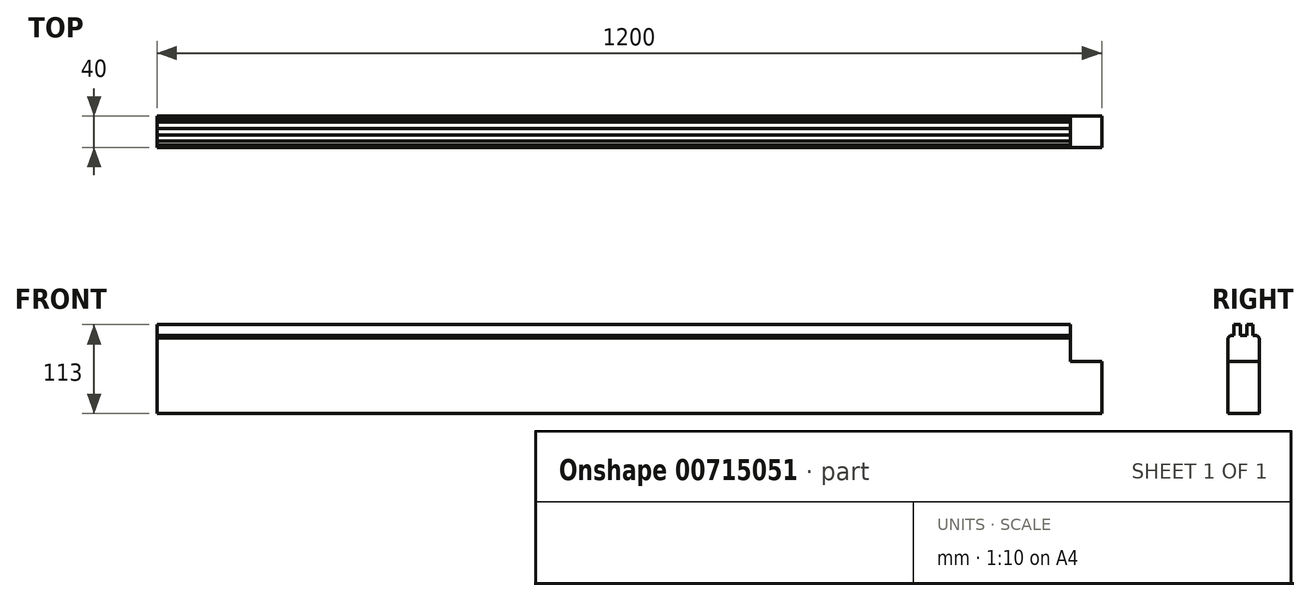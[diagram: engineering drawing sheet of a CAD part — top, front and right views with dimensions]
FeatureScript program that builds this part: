
annotation { "Feature Type Name" : "Feature", "Feature Type Description" : "" }
export const myFeature = defineFeature(function(context is Context, id is Id, definition is map)
    precondition{}
    {
        {
            assignVariable(context, id + "F0", {"name" : "Laenge", "anyValue" : 1200});
        }
        {
            var Q0;
            Q0=qCreatedBy(makeId("Right.planeOp"),FACE);
            var sketch = newSketch(context, id + "F1", { "sketchPlane" : qUnion([Q0])});
            skLineSegment(sketch, "E0", {"start": v(20, 63) * mm, "end": v(20, -63) * mm});
            skLineSegment(sketch, "E1", {"start": v(20, -63) * mm, "end": v(17, -66) * mm});
            skLineSegment(sketch, "E2", {"start": v(17, -66) * mm, "end": v(12, -66) * mm});
            skLineSegment(sketch, "E3", {"start": v(12, -52) * mm, "end": v(12, -66) * mm});
            skLineSegment(sketch, "E4", {"start": v(12, -52) * mm, "end": v(4, -52) * mm});
            skLineSegment(sketch, "E5", {"start": v(4, -66) * mm, "end": v(4, -52) * mm});
            skLineSegment(sketch, "E6", {"start": v(4, -66) * mm, "end": v(-4, -66) * mm});
            skLineSegment(sketch, "E7", {"start": v(-4, -52) * mm, "end": v(-4, -66) * mm});
            skLineSegment(sketch, "E8", {"start": v(-4, -52) * mm, "end": v(-12, -52) * mm});
            skLineSegment(sketch, "E9", {"start": v(-12, -66) * mm, "end": v(-12, -52) * mm});
            skLineSegment(sketch, "E10", {"start": v(-12, -66) * mm, "end": v(-17, -66) * mm});
            skLineSegment(sketch, "E11", {"start": v(-17, -66) * mm, "end": v(-20, -63) * mm});
            skLineSegment(sketch, "E12", {"start": v(-20, -63) * mm, "end": v(-20, 63) * mm});
            skLineSegment(sketch, "E13", {"start": v(-20, 63) * mm, "end": v(-17, 66) * mm});
            skLineSegment(sketch, "E14", {"start": v(-17, 66) * mm, "end": v(-12, 66) * mm});
            skLineSegment(sketch, "E15", {"start": v(-4, 66) * mm, "end": v(4, 66) * mm});
            skLineSegment(sketch, "E16", {"start": v(12, 66) * mm, "end": v(17, 66) * mm});
            skLineSegment(sketch, "E17", {"start": v(17, 66) * mm, "end": v(20, 63) * mm});
            skPoint(sketch, "E18.end.orphan", {"position": v(12, 57.8) * mm});
            skPoint(sketch, "E19.end.orphan", {"position": v(4, 66.3) * mm});
            skPoint(sketch, "E20.end.orphan", {"position": v(-4, 66.3) * mm});
            skLineSegment(sketch, "E21", {"start": v(-12, 66) * mm, "end": v(-12, 80) * mm});
            skLineSegment(sketch, "E22", {"start": v(-12, 80) * mm, "end": v(-4, 80) * mm});
            skLineSegment(sketch, "E23", {"start": v(-4, 80) * mm, "end": v(-4, 66) * mm});
            skLineSegment(sketch, "E24", {"start": v(4, 66) * mm, "end": v(4, 80) * mm});
            skLineSegment(sketch, "E25", {"start": v(4, 80) * mm, "end": v(12, 80) * mm});
            skLineSegment(sketch, "E26", {"start": v(12, 80) * mm, "end": v(12, 66) * mm});
            skLineSegment(sketch, "E27", {"start": v(20, -33) * mm, "end": v(-20, -33) * mm});
            skLineSegment(sketch, "E28", {"start": v(20, 33) * mm, "end": v(-20, 33) * mm});
            skPoint(sketch, "E29.end.orphan", {"position": v(-141.42, 0) * mm});
            skLineSegment(sketch, "E30", {"start": v(20, 0) * mm, "end": v(-20, 0) * mm});
            skLineSegment(sketch, "E31", {"start": v(20, 0) * mm, "end": v(-20, 0) * mm, "construction": true});
            skLineSegment(sketch, "E32", {"start": v(0, 33) * mm, "end": v(0, -33) * mm, "construction": true});
            skSolve(sketch);
        }
        {
            var Q0;
            Q0=qCreatedBy(makeId("Front.planeOp"),FACE);
            var sketch = newSketch(context, id + "F2", { "sketchPlane" : qUnion([Q0])});
            skLineSegment(sketch, "E33", {"start": v(600, 0) * mm, "end": v(-600, 0) * mm, "construction": true});
            skPoint(sketch, "E34.right.start.orphan", {"position": v(-259.12, 108.1) * mm});
            skPoint(sketch, "E35.left.start.orphan", {"position": v(237.35, 108.1) * mm});
            skPoint(sketch, "E36.left.end.orphan", {"position": v(237.35, -84.05) * mm});
            skPoint(sketch, "E36.bottom.start.orphan", {"position": v(237.35, -117.05) * mm});
            skPoint(sketch, "E37.right.start.orphan", {"position": v(-259.12, -117.05) * mm});
            skPoint(sketch, "E37.top.end.orphan", {"position": v(-259.12, -84.05) * mm});
            skLineSegment(sketch, "E38.bottom", {"start": v(-640, 33) * mm, "end": v(-560, 33) * mm});
            skLineSegment(sketch, "E38.top", {"start": v(-640, 133) * mm, "end": v(-560, 133) * mm});
            skLineSegment(sketch, "E38.left", {"start": v(-640, 33) * mm, "end": v(-640, 133) * mm});
            skLineSegment(sketch, "E38.right", {"start": v(-560, 33) * mm, "end": v(-560, 133) * mm});
            skPoint(sketch, "E38.middle", {"position": v(-600, 83) * mm});
            skLineSegment(sketch, "E39.bottom", {"start": v(-640, -133) * mm, "end": v(-560, -133) * mm});
            skLineSegment(sketch, "E39.top", {"start": v(-640, -33) * mm, "end": v(-560, -33) * mm});
            skLineSegment(sketch, "E39.left", {"start": v(-640, -133) * mm, "end": v(-640, -33) * mm});
            skLineSegment(sketch, "E39.right", {"start": v(-560, -133) * mm, "end": v(-560, -33) * mm});
            skPoint(sketch, "E39.middle", {"position": v(-600, -83) * mm});
            skLineSegment(sketch, "E40.bottom", {"start": v(640, 33) * mm, "end": v(560, 33) * mm});
            skLineSegment(sketch, "E40.top", {"start": v(640, 133) * mm, "end": v(560, 133) * mm});
            skLineSegment(sketch, "E40.left", {"start": v(640, 33) * mm, "end": v(640, 133) * mm});
            skLineSegment(sketch, "E40.right", {"start": v(560, 33) * mm, "end": v(560, 133) * mm});
            skPoint(sketch, "E40.middle", {"position": v(600, 83) * mm});
            skLineSegment(sketch, "E41.bottom", {"start": v(640, -33) * mm, "end": v(560, -33) * mm});
            skLineSegment(sketch, "E41.top", {"start": v(640, -133) * mm, "end": v(560, -133) * mm});
            skLineSegment(sketch, "E41.left", {"start": v(640, -33) * mm, "end": v(640, -133) * mm});
            skLineSegment(sketch, "E41.right", {"start": v(560, -33) * mm, "end": v(560, -133) * mm});
            skPoint(sketch, "E41.middle", {"position": v(600, -83) * mm});
            skSolve(sketch);
        }
        {
            var Q0;
            {var subQ3=sQuery(id+"F1.wireOp",EDGE,"E13");Q0=makeQuery(id+"F1.imprint","IMPRINT",FACE,{"disambiguationData":[TD([[makeQuery(id+"F1.imprint","IMPRINT",EDGE,{"derivedFrom":subQ3}),-1.0]])]});}
            var Q1;
            {var subQ0=sQuery(id+"F1.wireOp",EDGE,"E28");Q1=makeQuery(id+"F1.imprint","IMPRINT",FACE,{"disambiguationData":[TD([[makeQuery(id+"F1.imprint","IMPRINT",EDGE,{"derivedFrom":subQ0}),1.0]])]});}
            var Q2;
            {var subQ0=sQuery(id+"F1.wireOp",EDGE,"E27");Q2=makeQuery(id+"F1.imprint","IMPRINT",FACE,{"disambiguationData":[TD([[makeQuery(id+"F1.imprint","IMPRINT",EDGE,{"derivedFrom":subQ0}),-1.0]])]});}
            var Q3;
            {var subQ1=sQuery(id+"F1.wireOp",EDGE,"E1");Q3=makeQuery(id+"F1.imprint","IMPRINT",FACE,{"disambiguationData":[TD([[makeQuery(id+"F1.imprint","IMPRINT",EDGE,{"derivedFrom":subQ1}),-1.0]])]});}
            extrude(context, id + "F3", {"entities" : qUnion([Q0, Q1, Q2, Q3]), "endBound" : BoundingType.SYMMETRIC, "depth" : getVariable(context, 'Laenge') * mm, "offsetDistance" : 25 * mm});
        }
        {
            var Q0;
            Q0=makeQuery(id+"F2.imprint","IMPRINT",FACE,{"disambiguationData":[TD([[makeQuery(id+"F2.imprint","IMPRINT",EDGE,{"derivedFrom":sQuery(id+"F2.wireOp",EDGE,"E40.bottom")}),-1.0]])]});
            var Q1;
            Q1=makeQuery(id+"F2.imprint","IMPRINT",FACE,{"disambiguationData":[TD([[makeQuery(id+"F2.imprint","IMPRINT",EDGE,{"derivedFrom":sQuery(id+"F2.wireOp",EDGE,"E41.bottom")}),1.0]])]});
            extrude(context, id + "F4", {"entities" : qUnion([Q0, Q1]), "operationType" : NewBodyOperationType.REMOVE, "endBound" : BoundingType.SYMMETRIC, "oppositeDirection" : true, "depth" : 50 * mm, "offsetDistance" : 25 * mm});
        }
        {
            var Q0;
            Q0=makeQuery(id+"F3.opExtrude","SWEPT_FACE",FACE,{"disambiguationData":[OSD([sQuery(id+"F1.wireOp",EDGE,"E12")])]});
            var sketch = newSketch(context, id + "F5", { "sketchPlane" : qUnion([Q0])});
            skLineSegment(sketch, "E42.bottom", {"start": v(600, -33) * mm, "end": v(-600, -33) * mm});
            skLineSegment(sketch, "E42.top", {"start": v(600, -83) * mm, "end": v(-600, -83) * mm});
            skLineSegment(sketch, "E42.left", {"start": v(600, -33) * mm, "end": v(600, -83) * mm});
            skLineSegment(sketch, "E42.right", {"start": v(-600, -33) * mm, "end": v(-600, -83) * mm});
            skSolve(sketch);
        }
        {
            var Q0;
            {var subQ3=sQuery(id+"F5.wireOp",EDGE,"E42.top");Q0=makeQuery(id+"F5.imprint","IMPRINT",FACE,{"disambiguationData":[TD([[makeQuery(id+"F5.imprint","IMPRINT",EDGE,{"derivedFrom":subQ3}),-1.0]])]});}
            var Q1;
            {var subQ1=sQuery(id+"F1.wireOp",EDGE,"E12");var subQ5=makeQuery(id+"F3.opExtrude","SWEPT_EDGE",EDGE,{"disambiguationData":[OSD([sQuery(id+"F1.wireOp",EDGE,"E11"),subQ1])]});Q1=makeQuery(id+"F5.imprint","IMPRINT",FACE,{"disambiguationData":[TD([[makeQuery(id+"F5.imprint","IMPRINT",EDGE,{"derivedFrom":subQ5}),-1.0]])]});}
            extrude(context, id + "F6", {"entities" : qUnion([Q0, Q1]), "operationType" : NewBodyOperationType.REMOVE, "endBound" : BoundingType.UP_TO_NEXT, "oppositeDirection" : true, "depth" : 25 * mm, "offsetDistance" : 25 * mm});
        }
    });
